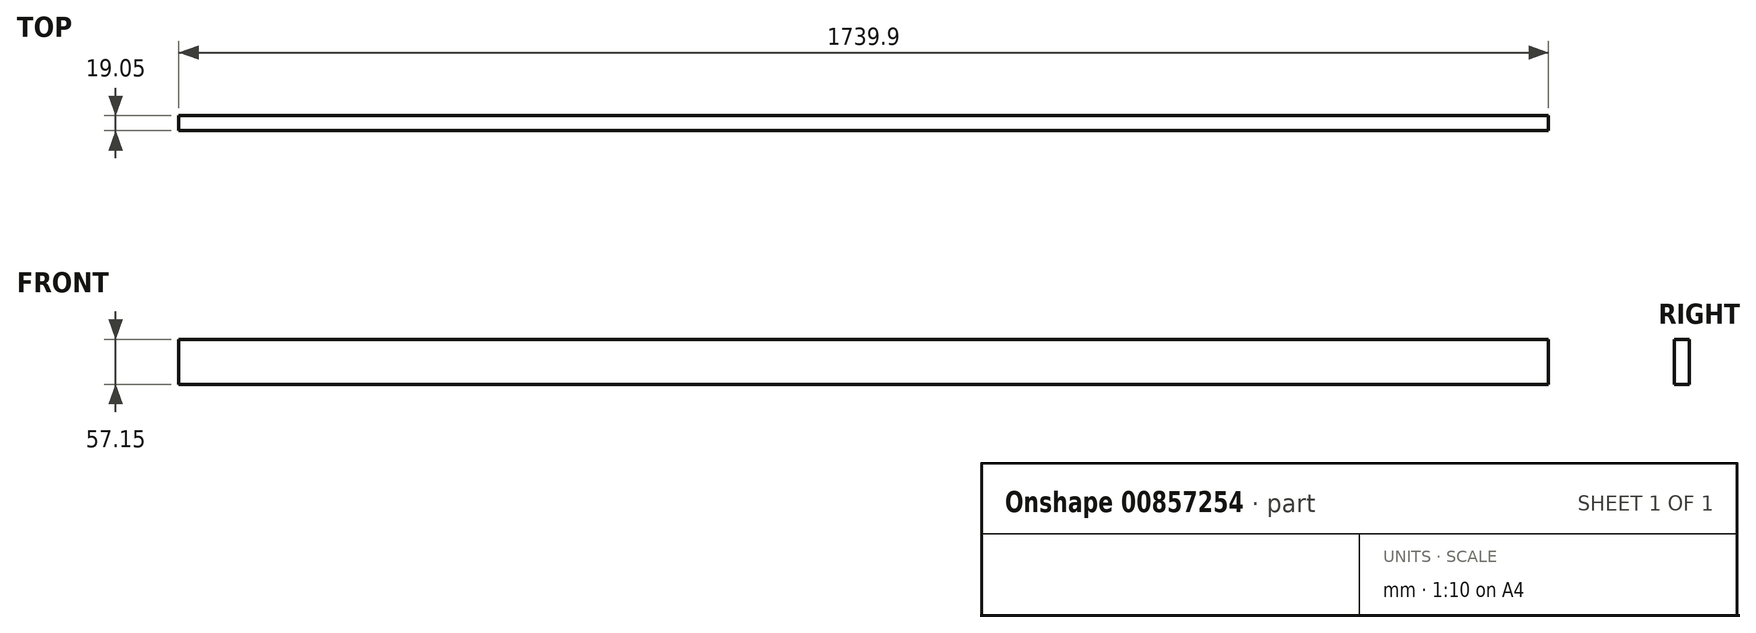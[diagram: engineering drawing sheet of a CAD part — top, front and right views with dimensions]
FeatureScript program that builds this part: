
annotation { "Feature Type Name" : "Feature", "Feature Type Description" : "" }
export const myFeature = defineFeature(function(context is Context, id is Id, definition is map)
    precondition{}
    {
        {
            var Q0;
            Q0=qCreatedBy(makeId("Front.planeOp"),FACE);
            var sketch = newSketch(context, id + "F0", { "sketchPlane" : qUnion([Q0])});
            skLineSegment(sketch, "E0.bottom", {"start": v(-1712.93, 51.42) * mm, "end": v(26.97, 51.42) * mm});
            skLineSegment(sketch, "E0.top", {"start": v(-1712.93, -5.73) * mm, "end": v(26.97, -5.73) * mm});
            skLineSegment(sketch, "E0.left", {"start": v(-1712.93, 51.42) * mm, "end": v(-1712.93, -5.73) * mm});
            skLineSegment(sketch, "E0.right", {"start": v(26.97, 51.42) * mm, "end": v(26.97, -5.73) * mm});
            skSolve(sketch);
        }
        {
            var Q0;
            Q0=makeQuery(id+"F0.imprint","IMPRINT",FACE,{"disambiguationData":[TD([[makeQuery(id+"F0.imprint","IMPRINT",EDGE,{"derivedFrom":sQuery(id+"F0.wireOp",EDGE,"E0.bottom")}),-1.0]])]});
            extrude(context, id + "F1", {"entities" : qUnion([Q0]), "depth" : 19.05 * mm, "offsetDistance" : 25.4 * mm});
        }
    });
